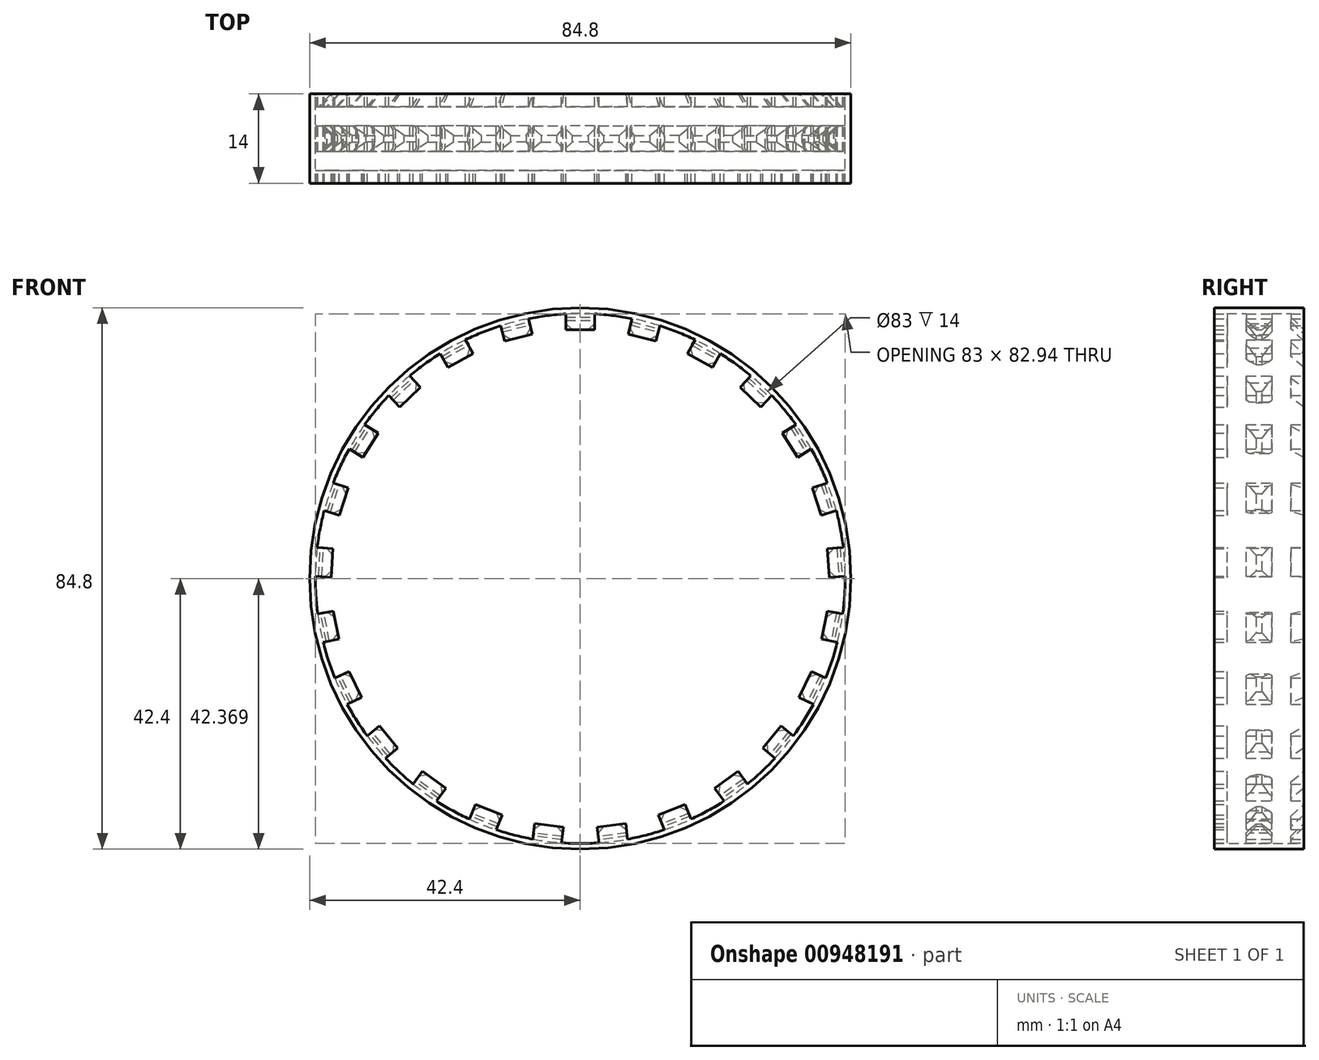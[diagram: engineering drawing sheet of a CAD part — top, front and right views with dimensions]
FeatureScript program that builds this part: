
annotation { "Feature Type Name" : "Feature", "Feature Type Description" : "" }
export const myFeature = defineFeature(function(context is Context, id is Id, definition is map)
    precondition{}
    {
        {
            var Q0;
            Q0=qCreatedBy(makeId("Top.planeOp"),FACE);
            var sketch = newSketch(context, id + "F0", { "sketchPlane" : qUnion([Q0])});
            skLineSegment(sketch, "E0", {"start": v(0, 44.68) * mm, "end": v(0, -51.28) * mm, "construction": true});
            skSolve(sketch);
        }
        {
            var Q0;
            Q0=qCreatedBy(makeId("Front.planeOp"),FACE);
            var sketch = newSketch(context, id + "F1", { "sketchPlane" : qUnion([Q0])});
            skCircle(sketch, "E1", {"center": v(0, 0) * mm, "radius": 41.5 * mm});
            skCircle(sketch, "E2", {"center": v(0, 0) * mm, "radius": 42.4 * mm});
            skLineSegment(sketch, "E3", {"start": v(0, 42.4) * mm, "end": v(0, 41.5) * mm, "construction": true});
            skPoint(sketch, "E4", {"position": v(0, 41.95) * mm});
            skCircle(sketch, "E5", {"center": v(0, 41.95) * mm, "radius": 2.25 * mm});
            skLineSegment(sketch, "E6.top", {"start": v(-2.25, 38.95) * mm, "end": v(2.25, 38.95) * mm});
            skLineSegment(sketch, "E6.left", {"start": v(-2.25, 41.44) * mm, "end": v(-2.25, 38.95) * mm});
            skLineSegment(sketch, "E6.right", {"start": v(2.25, 41.44) * mm, "end": v(2.25, 38.95) * mm});
            skPoint(sketch, "E7.orphan", {"position": v(2.25, 41.95) * mm});
            skPoint(sketch, "E8.orphan", {"position": v(-2.25, 41.95) * mm});
            skSolve(sketch);
        }
        {
            var Q0;
            {var subQ0=sQuery(id+"F1.wireOp",EDGE,"E1");var subQ2=makeQuery(id+"F1.imprint","INTERSECT",VERTEX,{"derivedFrom":[subQ0,sQuery(id+"F1.wireOp",EDGE,"E6.right")]});Q0=makeQuery(id+"F1.imprint","IMPRINT",FACE,{"disambiguationData":[TD([[makeQuery(id+"F1.imprint","IMPRINT",EDGE,{"disambiguationData":[TD([[subQ2,-1.0]])],"derivedFrom":subQ0}),-1.0]])]});}
            var Q1;
            {var subQ0=sQuery(id+"F1.wireOp",EDGE,"E5");var subQ1=sQuery(id+"F1.wireOp",EDGE,"E1");var subQ2=makeQuery(id+"F1.imprint","INTERSECT",VERTEX,{"disambiguationData":[OD(0.0)],"derivedFrom":[subQ1,subQ0]});Q1=makeQuery(id+"F1.imprint","IMPRINT",FACE,{"disambiguationData":[TD([[makeQuery(id+"F1.imprint","IMPRINT",EDGE,{"disambiguationData":[TD([[subQ2,-1.0]])],"derivedFrom":subQ1}),-1.0]])]});}
            extrude(context, id + "F2", {"entities" : qUnion([Q0, Q1]), "endBound" : BoundingType.SYMMETRIC, "depth" : 14 * mm, "offsetDistance" : 25 * mm});
        }
        {
            var Q0;
            {var subQ0=sQuery(id+"F1.wireOp",EDGE,"E5");var subQ1=sQuery(id+"F1.wireOp",EDGE,"E2");var subQ2=makeQuery(id+"F1.imprint","INTERSECT",VERTEX,{"disambiguationData":[OD(0.0)],"derivedFrom":[subQ1,subQ0]});Q0=makeQuery(id+"F1.imprint","IMPRINT",FACE,{"disambiguationData":[TD([[makeQuery(id+"F1.imprint","IMPRINT",EDGE,{"disambiguationData":[TD([[subQ2,1.0]])],"derivedFrom":subQ1}),-1.0]])]});}
            var Q1;
            {var subQ0=sQuery(id+"F1.wireOp",EDGE,"E5");var subQ1=sQuery(id+"F1.wireOp",EDGE,"E1");var subQ2=makeQuery(id+"F1.imprint","INTERSECT",VERTEX,{"disambiguationData":[OD(0.0)],"derivedFrom":[subQ1,subQ0]});Q1=makeQuery(id+"F1.imprint","IMPRINT",FACE,{"disambiguationData":[TD([[makeQuery(id+"F1.imprint","IMPRINT",EDGE,{"disambiguationData":[TD([[subQ2,-1.0]])],"derivedFrom":subQ1}),1.0]])]});}
            var Q2;
            {var subQ0=sQuery(id+"F1.wireOp",EDGE,"E6.right");Q2=makeQuery(id+"F1.imprint","IMPRINT",FACE,{"disambiguationData":[TD([[makeQuery(id+"F1.imprint","IMPRINT",EDGE,{"derivedFrom":subQ0}),-1.0]])]});}
            var Q3;
            {var subQ0=sQuery(id+"F1.wireOp",EDGE,"E6.left");Q3=makeQuery(id+"F1.imprint","IMPRINT",FACE,{"disambiguationData":[TD([[makeQuery(id+"F1.imprint","IMPRINT",EDGE,{"derivedFrom":subQ0}),1.0]])]});}
            var Q4;
            Q4=sQuery(id+"F1.wireOp",EDGE,"E5");
            extrude(context, id + "F3", {"entities" : qUnion([Q0, Q1, Q2, Q3]), "surfaceEntities" : qUnion([Q4]), "endBound" : BoundingType.SYMMETRIC, "depth" : 14 * mm, "offsetDistance" : 25 * mm});
        }
        {
            var Q0;
            {var subQ0=sQuery(id+"F1.wireOp",EDGE,"E5");var subQ1=sQuery(id+"F1.wireOp",EDGE,"E1");var subQ2=makeQuery(id+"F1.imprint","INTERSECT",VERTEX,{"disambiguationData":[OD(0.0)],"derivedFrom":[subQ1,subQ0]});Q0=makeQuery(id+"F1.imprint","IMPRINT",FACE,{"disambiguationData":[TD([[makeQuery(id+"F1.imprint","IMPRINT",EDGE,{"disambiguationData":[TD([[subQ2,1.0]])],"derivedFrom":subQ1}),1.0]])]});}
            var Q1;
            {var subQ0=sQuery(id+"F1.wireOp",EDGE,"E5");var subQ1=sQuery(id+"F1.wireOp",EDGE,"E1");var subQ2=makeQuery(id+"F1.imprint","INTERSECT",VERTEX,{"disambiguationData":[OD(0.0)],"derivedFrom":[subQ1,subQ0]});Q1=makeQuery(id+"F1.imprint","IMPRINT",FACE,{"disambiguationData":[TD([[makeQuery(id+"F1.imprint","IMPRINT",EDGE,{"disambiguationData":[TD([[subQ2,-1.0]])],"derivedFrom":subQ1}),1.0]])]});}
            var Q2;
            {var subQ0=sQuery(id+"F1.wireOp",EDGE,"E6.left");var subQ1=sQuery(id+"F1.wireOp",EDGE,"E1");var subQ2=makeQuery(id+"F1.imprint","INTERSECT",VERTEX,{"derivedFrom":[subQ1,subQ0]});Q2=makeQuery(id+"F1.imprint","IMPRINT",FACE,{"disambiguationData":[TD([[makeQuery(id+"F1.imprint","IMPRINT",EDGE,{"disambiguationData":[TD([[subQ2,1.0]])],"derivedFrom":subQ1}),1.0]])]});}
            var Q3;
            Q3=sQuery(id+"F1.wireOp",EDGE,"E5");
            extrude(context, id + "F4", {"entities" : qUnion([Q0, Q1, Q2]), "operationType" : NewBodyOperationType.REMOVE, "surfaceEntities" : qUnion([Q3]), "endBound" : BoundingType.SYMMETRIC, "oppositeDirection" : true, "depth" : 10 * mm, "offsetDistance" : 25 * mm});
        }
        {
            var Q0;
            Q0=makeQuery(id+"F4.boolean.opBoolean","COPY",EDGE,{"derivedFrom":makeQuery(id+"F4.opExtrude","CAP_EDGE",EDGE,{"disambiguationData":[OSD([sQuery(id+"F1.wireOp",EDGE,"E6.top")])],"isStart":false})});
            var Q1;
            Q1=makeQuery(id+"F4.boolean.opBoolean","COPY",EDGE,{"derivedFrom":makeQuery(id+"F4.opExtrude","CAP_EDGE",EDGE,{"disambiguationData":[OSD([sQuery(id+"F1.wireOp",EDGE,"E6.top")])],"isStart":true})});
            chamfer(context, id + "F5", {"entities" : qUnion([Q0, Q1]), "width" : 2 * mm, "tangentPropagation" : true});
        }
        {
            var Q0;
            {var subQ0=sQuery(id+"F1.wireOp",EDGE,"E5");var subQ1=sQuery(id+"F1.wireOp",EDGE,"E1");var subQ2=makeQuery(id+"F1.imprint","INTERSECT",VERTEX,{"disambiguationData":[OD(0.0)],"derivedFrom":[subQ1,subQ0]});Q0=makeQuery(id+"F1.imprint","IMPRINT",FACE,{"disambiguationData":[TD([[makeQuery(id+"F1.imprint","IMPRINT",EDGE,{"disambiguationData":[TD([[subQ2,1.0]])],"derivedFrom":subQ1}),1.0]])]});}
            var Q1;
            {var subQ0=sQuery(id+"F1.wireOp",EDGE,"E6.left");var subQ1=sQuery(id+"F1.wireOp",EDGE,"E1");var subQ2=makeQuery(id+"F1.imprint","INTERSECT",VERTEX,{"derivedFrom":[subQ1,subQ0]});Q1=makeQuery(id+"F1.imprint","IMPRINT",FACE,{"disambiguationData":[TD([[makeQuery(id+"F1.imprint","IMPRINT",EDGE,{"disambiguationData":[TD([[subQ2,1.0]])],"derivedFrom":subQ1}),1.0]])]});}
            var Q2;
            {var subQ0=sQuery(id+"F1.wireOp",EDGE,"E5");var subQ1=sQuery(id+"F1.wireOp",EDGE,"E1");var subQ2=makeQuery(id+"F1.imprint","INTERSECT",VERTEX,{"disambiguationData":[OD(0.0)],"derivedFrom":[subQ1,subQ0]});Q2=makeQuery(id+"F1.imprint","IMPRINT",FACE,{"disambiguationData":[TD([[makeQuery(id+"F1.imprint","IMPRINT",EDGE,{"disambiguationData":[TD([[subQ2,-1.0]])],"derivedFrom":subQ1}),1.0]])]});}
            extrude(context, id + "F6", {"entities" : qUnion([Q0, Q1, Q2]), "endBound" : BoundingType.SYMMETRIC, "depth" : 4 * mm, "offsetDistance" : 25 * mm});
        }
        {
            var Q0;
            Q0=makeQuery(id+"F6.opExtrude","CAP_EDGE",EDGE,{"disambiguationData":[OSD([sQuery(id+"F1.wireOp",EDGE,"E6.top")])],"isStart":true});
            var Q1;
            Q1=makeQuery(id+"F6.opExtrude","CAP_EDGE",EDGE,{"disambiguationData":[OSD([sQuery(id+"F1.wireOp",EDGE,"E6.top")])],"isStart":false});
            chamfer(context, id + "F7", {"entities" : qUnion([Q0, Q1]), "chamferType" : ChamferType.OFFSET_ANGLE, "width" : 1.5 * mm, "oppositeDirection" : false, "angle" : 45 * degree, "tangentPropagation" : true});
        }
        {
            var Q0;
            Q0=makeQuery(id+"F6.opExtrude","SWEPT_EDGE",EDGE,{"disambiguationData":[OSD([sQuery(id+"F1.wireOp",EDGE,"E6.top"),sQuery(id+"F1.wireOp",EDGE,"E6.left")])]});
            var Q1;
            Q1=makeQuery(id+"F6.opExtrude","SWEPT_EDGE",EDGE,{"disambiguationData":[OSD([sQuery(id+"F1.wireOp",EDGE,"E6.top"),sQuery(id+"F1.wireOp",EDGE,"E6.right")])]});
            chamfer(context, id + "F8", {"entities" : qUnion([Q0, Q1]), "width" : 1 * mm, "tangentPropagation" : true});
        }
        {
            var Q0;
            Q0=makeQuery(id+"F6.opExtrude","SWEPT_BODY",BODY,{"disambiguationData":[OSD([sQuery(id+"F1.wireOp",EDGE,"E1"),sQuery(id+"F1.wireOp",EDGE,"E6.top"),sQuery(id+"F1.wireOp",EDGE,"E6.left"),sQuery(id+"F1.wireOp",EDGE,"E6.right")])]});
            var Q1;
            Q1=makeQuery(id+"F4.boolean.opBoolean","SPLIT",BODY,{"disambiguationData":[OD(1.0)],"derivedFrom":makeQuery(id+"F3.opExtrude","SWEPT_BODY",BODY,{"disambiguationData":[OSD([sQuery(id+"F1.wireOp",EDGE,"E1"),sQuery(id+"F1.wireOp",EDGE,"E6.top"),sQuery(id+"F1.wireOp",EDGE,"E6.left"),sQuery(id+"F1.wireOp",EDGE,"E6.right")])]})});
            var Q2;
            Q2=makeQuery(id+"F4.boolean.opBoolean","SPLIT",BODY,{"disambiguationData":[OD(0.0)],"derivedFrom":makeQuery(id+"F3.opExtrude","SWEPT_BODY",BODY,{"disambiguationData":[OSD([sQuery(id+"F1.wireOp",EDGE,"E1"),sQuery(id+"F1.wireOp",EDGE,"E6.top"),sQuery(id+"F1.wireOp",EDGE,"E6.left"),sQuery(id+"F1.wireOp",EDGE,"E6.right")])]})});
            var Q3;
            Q3=makeQuery(id+"F3.opExtrude","SWEPT_BODY",BODY,{"disambiguationData":[OSD([sQuery(id+"F1.wireOp",EDGE,"E2"),sQuery(id+"F1.wireOp",EDGE,"E5")])]});
            var Q4;
            Q4=sQuery(id+"F0.wireOp",EDGE,"E0");
            var Q5;
            Q5=makeQuery(id+"F2.opExtrude","SWEPT_BODY",BODY,{"disambiguationData":[OSD([sQuery(id+"F1.wireOp",EDGE,"E1"),sQuery(id+"F1.wireOp",EDGE,"E2")])]});
            circularPattern(context, id + "F9", {"operationType" : NewBodyOperationType.ADD, "entities" : qUnion([Q0, Q1, Q2, Q3]), "axis" : qUnion([Q4]), "angle" : 360 * degree, "instanceCount" : 25, "equalSpace" : true});
        }
    });
